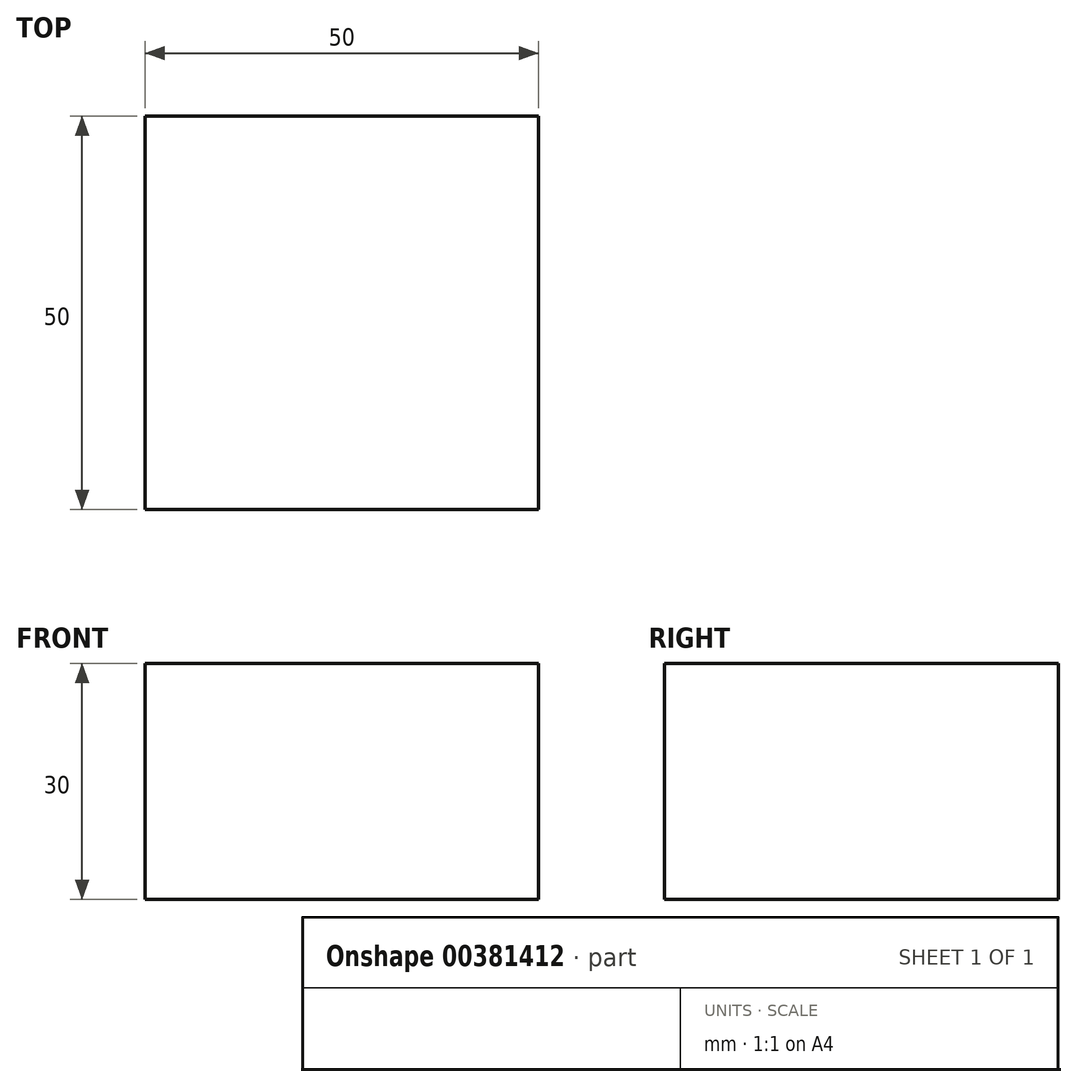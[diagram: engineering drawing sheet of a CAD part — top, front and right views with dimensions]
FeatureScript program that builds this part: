
annotation { "Feature Type Name" : "Feature", "Feature Type Description" : "" }
export const myFeature = defineFeature(function(context is Context, id is Id, definition is map)
    precondition{}
    {
        {
            var Q0;
            Q0=qCreatedBy(makeId("Top.planeOp"),FACE);
            var sketch = newSketch(context, id + "F0", { "sketchPlane" : qUnion([Q0])});
            skLineSegment(sketch, "E0.bottom", {"start": v(25, 25) * mm, "end": v(-25, 25) * mm});
            skLineSegment(sketch, "E0.top", {"start": v(25, -25) * mm, "end": v(-25, -25) * mm});
            skLineSegment(sketch, "E0.left", {"start": v(25, 25) * mm, "end": v(25, -25) * mm});
            skLineSegment(sketch, "E0.right", {"start": v(-25, 25) * mm, "end": v(-25, -25) * mm});
            skPoint(sketch, "E0.middle", {"position": v(0, 0) * mm});
            skSolve(sketch);
        }
        {
            var Q0;
            Q0=makeQuery(id+"F0.imprint","IMPRINT",FACE,{"disambiguationData":[TD([[makeQuery(id+"F0.imprint","IMPRINT",EDGE,{"derivedFrom":sQuery(id+"F0.wireOp",EDGE,"E0.bottom")}),1.0]])]});
            extrude(context, id + "F1", {"entities" : qUnion([Q0]), "depth" : 30 * mm});
        }
    });
